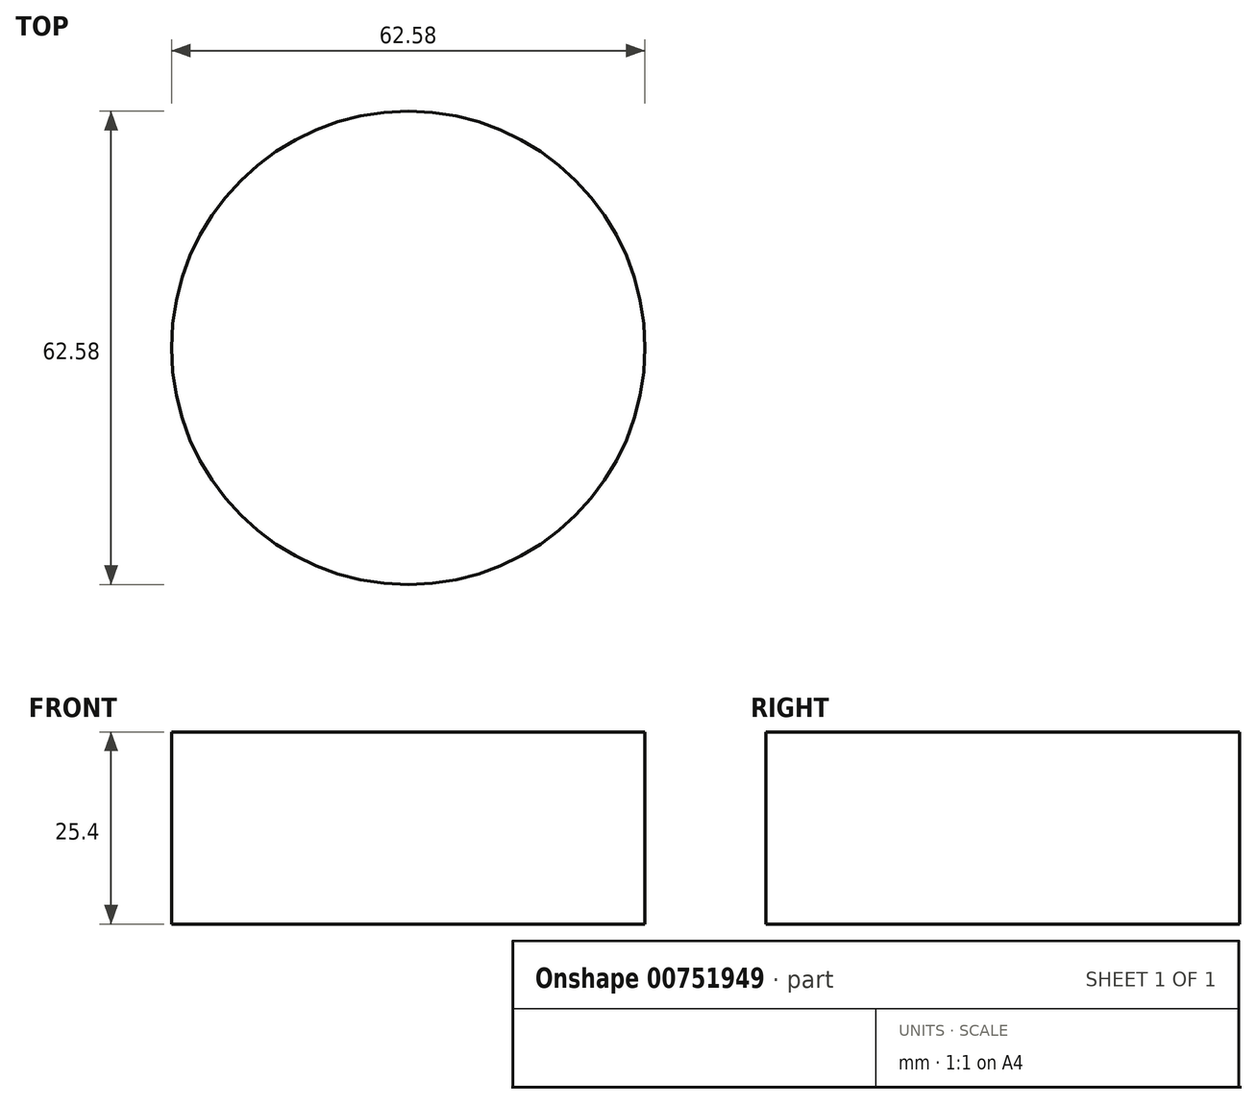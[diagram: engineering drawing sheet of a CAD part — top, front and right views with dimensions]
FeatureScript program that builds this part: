
annotation { "Feature Type Name" : "Feature", "Feature Type Description" : "" }
export const myFeature = defineFeature(function(context is Context, id is Id, definition is map)
    precondition{}
    {
        {
            var Q0;
            Q0=qCreatedBy(makeId("Top.planeOp"),FACE);
            var sketch = newSketch(context, id + "F0", { "sketchPlane" : qUnion([Q0])});
            skCircle(sketch, "E0", {"center": v(0, 0) * mm, "radius": 31.3 * mm});
            skSolve(sketch);
        }
        {
            var Q0;
            Q0 = qSketchRegion(id + "F0", true);
            extrude(context, id + "F1", {"entities" : qUnion([Q0]), "depth" : 25.4 * mm, "offsetDistance" : 25.4 * mm});
        }
    });
